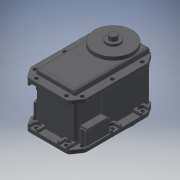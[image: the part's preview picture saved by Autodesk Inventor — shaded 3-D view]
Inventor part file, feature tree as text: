
AUTODESK INVENTOR PART (.ipt)
format: ipt  version: 2019 (Build 230136000, 136)  size: 816,128 bytes
history: native  units: mm
features: other x2, extrude x2, sketch x2
ambient origin geometry x8: Origin, YZ Plane, XZ Plane, XY Plane, X Axis, Y Axis, Z Axis, Center Point
bodies: Body1 (feature_tree)
feature tree (6):
  other  "솔리드1"
  other  "기준1"
  extrude  "돌출1"  Depth=11.0mm
  extrude  "돌출2"  Depth=2.5mm
  sketch  "스케치1"
  sketch  "스케치2"
